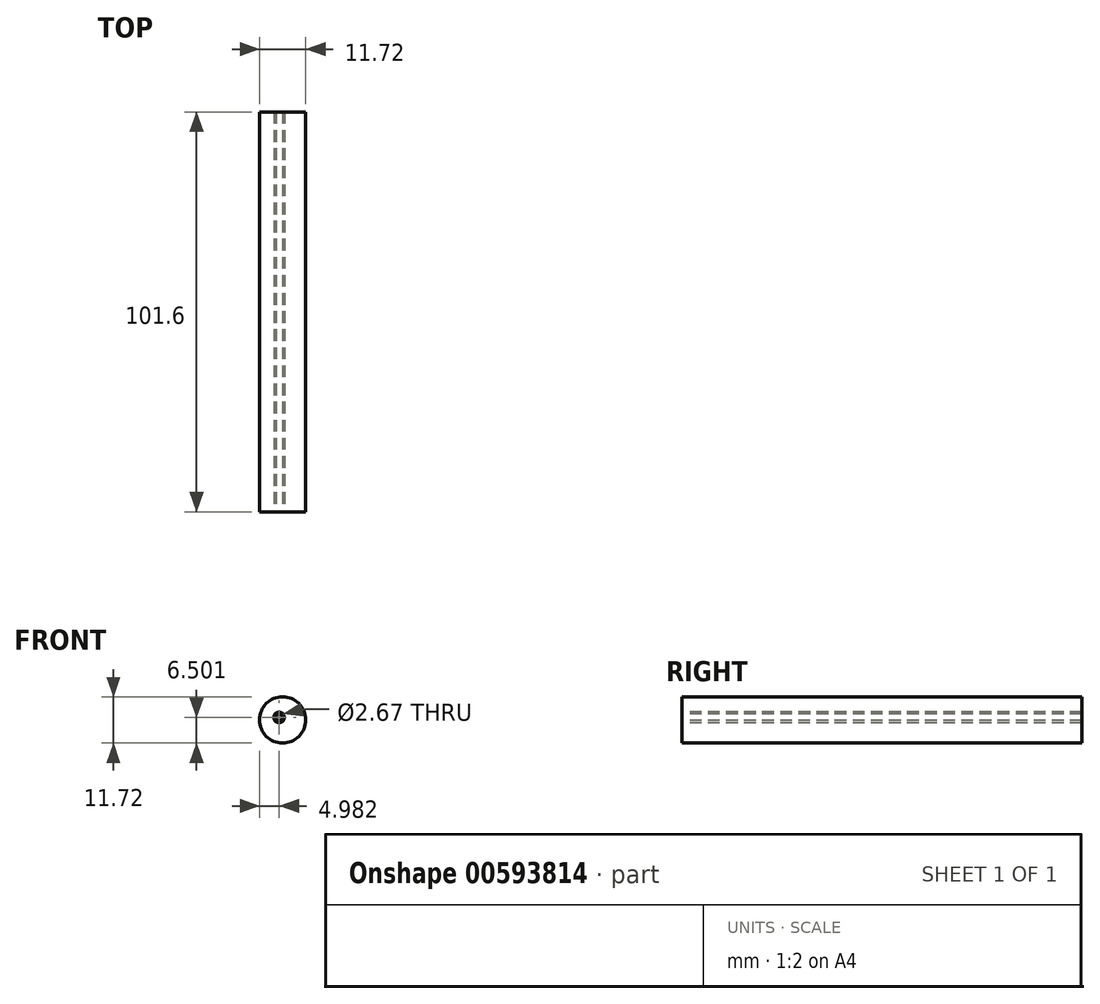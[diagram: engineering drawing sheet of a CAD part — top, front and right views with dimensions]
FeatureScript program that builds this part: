
annotation { "Feature Type Name" : "Feature", "Feature Type Description" : "" }
export const myFeature = defineFeature(function(context is Context, id is Id, definition is map)
    precondition{}
    {
        {
            var Q0;
            Q0=qCreatedBy(makeId("Front.planeOp"),FACE);
            var sketch = newSketch(context, id + "F0", { "sketchPlane" : qUnion([Q0])});
            skCircle(sketch, "E0", {"center": v(0, 0) * mm, "radius": 5.86 * mm});
            skSolve(sketch);
        }
        {
            var Q0;
            Q0 = qSketchRegion(id + "F0", true);
            extrude(context, id + "F1", {"entities" : qUnion([Q0]), "depth" : 101.6 * mm, "offsetDistance" : 25.4 * mm});
        }
        {
            var Q0;
            Q0=makeQuery(id+"F1.opExtrude","CAP_FACE",FACE,{"disambiguationData":[OSD([sQuery(id+"F0.wireOp",EDGE,"E0")])],"isStart":false});
            var sketch = newSketch(context, id + "F2", { "sketchPlane" : qUnion([Q0])});
            skCircle(sketch, "E1", {"center": v(-0.88, 0.64) * mm, "radius": 1.34 * mm});
            skCircle(sketch, "E2", {"center": v(-0.88, 0.64) * mm, "radius": 0.82 * mm});
            skSolve(sketch);
        }
        {
            var Q0;
            Q0=makeQuery(id+"F2.imprint","IMPRINT",FACE,{"disambiguationData":[TD([[makeQuery(id+"F2.imprint","IMPRINT",EDGE,{"derivedFrom":sQuery(id+"F2.wireOp",EDGE,"E1")}),1.0]])]});
            extrude(context, id + "F3", {"entities" : qUnion([Q0]), "operationType" : NewBodyOperationType.REMOVE, "oppositeDirection" : true, "depth" : 101.6 * mm, "offsetDistance" : 25.4 * mm});
        }
    });
